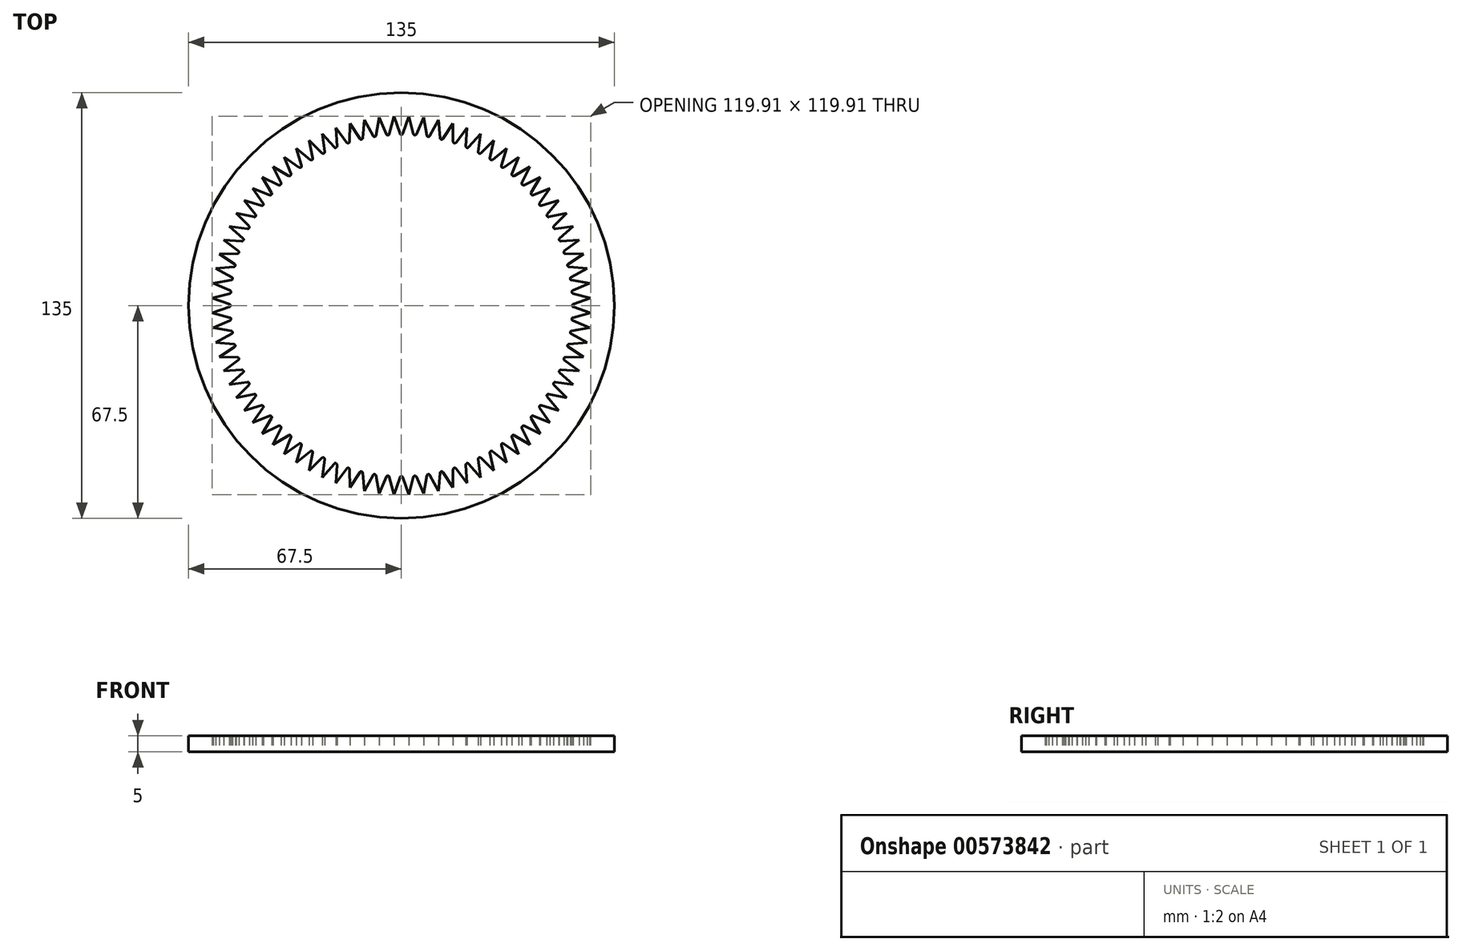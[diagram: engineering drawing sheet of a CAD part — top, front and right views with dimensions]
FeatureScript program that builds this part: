
annotation { "Feature Type Name" : "Feature", "Feature Type Description" : "" }
export const myFeature = defineFeature(function(context is Context, id is Id, definition is map)
    precondition{}
    {
        {
            var Q0;
            Q0=qCreatedBy(makeId("Top.planeOp"),FACE);
            var sketch = newSketch(context, id + "F0", { "sketchPlane" : qUnion([Q0])});
            skLineSegment(sketch, "E0", {"start": v(-2.35, 59.95) * mm, "end": v(-0.47, 54.5) * mm});
            skLineSegment(sketch, "E1", {"start": v(0.47, 54.5) * mm, "end": v(2.36, 59.95) * mm});
            skPoint(sketch, "E2", {"position": v(0, 60) * mm});
            skCircle(sketch, "E3", {"center": v(0, 0) * mm, "radius": 67.5 * mm});
            skPoint(sketch, "E4.visualSharp", {"position": v(0, 53.14) * mm});
            skArc(sketch, "E4.filletArc", {"start": v(-0.47, 54.5) * mm, "mid": v(0, 54.17) * mm, "end": v(0.47, 54.5) * mm});
            skLineSegment(sketch, "E5.1.0", {"start": v(-3.8, 54.38) * mm, "end": v(-2.36, 59.95) * mm});
            skLineSegment(sketch, "E5.1.1", {"start": v(-7.05, 59.58) * mm, "end": v(-4.75, 54.3) * mm});
            skArc(sketch, "E5.1.2", {"start": v(-4.75, 54.3) * mm, "mid": v(-4.25, 54) * mm, "end": v(-3.8, 54.38) * mm});
            skLineSegment(sketch, "E5.2.0", {"start": v(-8.06, 53.9) * mm, "end": v(-7.05, 59.58) * mm});
            skLineSegment(sketch, "E5.2.1", {"start": v(-11.7, 58.85) * mm, "end": v(-9, 53.76) * mm});
            skArc(sketch, "E5.2.2", {"start": v(-9, 53.76) * mm, "mid": v(-8.47, 53.5) * mm, "end": v(-8.06, 53.9) * mm});
            skLineSegment(sketch, "E5.3.0", {"start": v(-12.26, 53.11) * mm, "end": v(-11.7, 58.85) * mm});
            skLineSegment(sketch, "E5.3.1", {"start": v(-16.29, 57.75) * mm, "end": v(-13.18, 52.9) * mm});
            skArc(sketch, "E5.3.2", {"start": v(-13.18, 52.9) * mm, "mid": v(-12.65, 52.67) * mm, "end": v(-12.26, 53.11) * mm});
            skLineSegment(sketch, "E5.4.0", {"start": v(-16.4, 51.98) * mm, "end": v(-16.29, 57.75) * mm});
            skLineSegment(sketch, "E5.4.1", {"start": v(-20.77, 56.3) * mm, "end": v(-17.3, 51.7) * mm});
            skArc(sketch, "E5.4.2", {"start": v(-17.3, 51.7) * mm, "mid": v(-16.74, 51.52) * mm, "end": v(-16.4, 51.98) * mm});
            skLineSegment(sketch, "E5.5.0", {"start": v(-20.42, 50.54) * mm, "end": v(-20.77, 56.3) * mm});
            skLineSegment(sketch, "E5.5.1", {"start": v(-25.12, 54.49) * mm, "end": v(-21.3, 50.18) * mm});
            skArc(sketch, "E5.5.2", {"start": v(-21.3, 50.18) * mm, "mid": v(-20.73, 50.05) * mm, "end": v(-20.42, 50.54) * mm});
            skLineSegment(sketch, "E5.6.0", {"start": v(-24.32, 48.78) * mm, "end": v(-25.12, 54.49) * mm});
            skLineSegment(sketch, "E5.6.1", {"start": v(-29.32, 52.35) * mm, "end": v(-25.17, 48.35) * mm});
            skArc(sketch, "E5.6.2", {"start": v(-25.17, 48.35) * mm, "mid": v(-24.6, 48.27) * mm, "end": v(-24.32, 48.78) * mm});
            skLineSegment(sketch, "E5.7.0", {"start": v(-28.08, 46.72) * mm, "end": v(-29.32, 52.35) * mm});
            skLineSegment(sketch, "E5.7.1", {"start": v(-33.33, 49.89) * mm, "end": v(-28.88, 46.23) * mm});
            skArc(sketch, "E5.7.2", {"start": v(-28.88, 46.23) * mm, "mid": v(-28.3, 46.19) * mm, "end": v(-28.08, 46.72) * mm});
            skLineSegment(sketch, "E5.8.0", {"start": v(-31.66, 44.37) * mm, "end": v(-33.33, 49.89) * mm});
            skLineSegment(sketch, "E5.8.1", {"start": v(-37.15, 47.12) * mm, "end": v(-32.42, 43.82) * mm});
            skArc(sketch, "E5.8.2", {"start": v(-32.42, 43.82) * mm, "mid": v(-31.84, 43.82) * mm, "end": v(-31.66, 44.37) * mm});
            skLineSegment(sketch, "E5.9.0", {"start": v(-35.04, 41.75) * mm, "end": v(-37.15, 47.12) * mm});
            skLineSegment(sketch, "E5.9.1", {"start": v(-40.73, 44.06) * mm, "end": v(-35.76, 41.14) * mm});
            skArc(sketch, "E5.9.2", {"start": v(-35.76, 41.14) * mm, "mid": v(-35.18, 41.2) * mm, "end": v(-35.04, 41.75) * mm});
            skLineSegment(sketch, "E5.10.0", {"start": v(-38.2, 38.88) * mm, "end": v(-40.73, 44.06) * mm});
            skLineSegment(sketch, "E5.10.1", {"start": v(-44.06, 40.73) * mm, "end": v(-38.88, 38.2) * mm});
            skArc(sketch, "E5.10.2", {"start": v(-38.88, 38.2) * mm, "mid": v(-38.3, 38.3) * mm, "end": v(-38.2, 38.88) * mm});
            skLineSegment(sketch, "E5.11.0", {"start": v(-41.14, 35.76) * mm, "end": v(-44.06, 40.73) * mm});
            skLineSegment(sketch, "E5.11.1", {"start": v(-47.12, 37.15) * mm, "end": v(-41.75, 35.04) * mm});
            skArc(sketch, "E5.11.2", {"start": v(-41.75, 35.04) * mm, "mid": v(-41.2, 35.18) * mm, "end": v(-41.14, 35.76) * mm});
            skLineSegment(sketch, "E5.12.0", {"start": v(-43.82, 32.42) * mm, "end": v(-47.12, 37.15) * mm});
            skLineSegment(sketch, "E5.12.1", {"start": v(-49.89, 33.33) * mm, "end": v(-44.37, 31.66) * mm});
            skArc(sketch, "E5.12.2", {"start": v(-44.37, 31.66) * mm, "mid": v(-43.82, 31.84) * mm, "end": v(-43.82, 32.42) * mm});
            skLineSegment(sketch, "E5.13.0", {"start": v(-46.23, 28.88) * mm, "end": v(-49.89, 33.33) * mm});
            skLineSegment(sketch, "E5.13.1", {"start": v(-52.35, 29.32) * mm, "end": v(-46.72, 28.08) * mm});
            skArc(sketch, "E5.13.2", {"start": v(-46.72, 28.08) * mm, "mid": v(-46.19, 28.3) * mm, "end": v(-46.23, 28.88) * mm});
            skLineSegment(sketch, "E5.14.0", {"start": v(-48.35, 25.17) * mm, "end": v(-52.35, 29.32) * mm});
            skLineSegment(sketch, "E5.14.1", {"start": v(-54.49, 25.12) * mm, "end": v(-48.78, 24.32) * mm});
            skArc(sketch, "E5.14.2", {"start": v(-48.78, 24.32) * mm, "mid": v(-48.27, 24.6) * mm, "end": v(-48.35, 25.17) * mm});
            skLineSegment(sketch, "E5.15.0", {"start": v(-50.18, 21.3) * mm, "end": v(-54.49, 25.12) * mm});
            skLineSegment(sketch, "E5.15.1", {"start": v(-56.3, 20.77) * mm, "end": v(-50.54, 20.42) * mm});
            skArc(sketch, "E5.15.2", {"start": v(-50.54, 20.42) * mm, "mid": v(-50.05, 20.73) * mm, "end": v(-50.18, 21.3) * mm});
            skLineSegment(sketch, "E5.16.0", {"start": v(-51.7, 17.3) * mm, "end": v(-56.3, 20.77) * mm});
            skLineSegment(sketch, "E5.16.1", {"start": v(-57.75, 16.29) * mm, "end": v(-51.98, 16.4) * mm});
            skArc(sketch, "E5.16.2", {"start": v(-51.98, 16.4) * mm, "mid": v(-51.52, 16.74) * mm, "end": v(-51.7, 17.3) * mm});
            skLineSegment(sketch, "E5.17.0", {"start": v(-52.9, 13.18) * mm, "end": v(-57.75, 16.29) * mm});
            skLineSegment(sketch, "E5.17.1", {"start": v(-58.85, 11.7) * mm, "end": v(-53.11, 12.26) * mm});
            skArc(sketch, "E5.17.2", {"start": v(-53.11, 12.26) * mm, "mid": v(-52.67, 12.65) * mm, "end": v(-52.9, 13.18) * mm});
            skLineSegment(sketch, "E5.18.0", {"start": v(-53.76, 9) * mm, "end": v(-58.85, 11.7) * mm});
            skLineSegment(sketch, "E5.18.1", {"start": v(-59.58, 7.05) * mm, "end": v(-53.9, 8.06) * mm});
            skArc(sketch, "E5.18.2", {"start": v(-53.9, 8.06) * mm, "mid": v(-53.5, 8.47) * mm, "end": v(-53.76, 9) * mm});
            skLineSegment(sketch, "E5.19.0", {"start": v(-54.3, 4.75) * mm, "end": v(-59.58, 7.05) * mm});
            skLineSegment(sketch, "E5.19.1", {"start": v(-59.95, 2.36) * mm, "end": v(-54.38, 3.8) * mm});
            skArc(sketch, "E5.19.2", {"start": v(-54.38, 3.8) * mm, "mid": v(-54, 4.25) * mm, "end": v(-54.3, 4.75) * mm});
            skLineSegment(sketch, "E5.20.0", {"start": v(-54.5, 0.47) * mm, "end": v(-59.95, 2.36) * mm});
            skLineSegment(sketch, "E5.20.1", {"start": v(-59.95, -2.35) * mm, "end": v(-54.5, -0.47) * mm});
            skArc(sketch, "E5.20.2", {"start": v(-54.5, -0.47) * mm, "mid": v(-54.17, 0) * mm, "end": v(-54.5, 0.47) * mm});
            skLineSegment(sketch, "E5.21.0", {"start": v(-54.38, -3.8) * mm, "end": v(-59.95, -2.36) * mm});
            skLineSegment(sketch, "E5.21.1", {"start": v(-59.58, -7.05) * mm, "end": v(-54.3, -4.75) * mm});
            skArc(sketch, "E5.21.2", {"start": v(-54.3, -4.75) * mm, "mid": v(-54, -4.25) * mm, "end": v(-54.38, -3.8) * mm});
            skLineSegment(sketch, "E5.22.0", {"start": v(-53.9, -8.06) * mm, "end": v(-59.58, -7.05) * mm});
            skLineSegment(sketch, "E5.22.1", {"start": v(-58.85, -11.7) * mm, "end": v(-53.76, -9) * mm});
            skArc(sketch, "E5.22.2", {"start": v(-53.76, -9) * mm, "mid": v(-53.5, -8.47) * mm, "end": v(-53.9, -8.06) * mm});
            skLineSegment(sketch, "E5.23.0", {"start": v(-53.11, -12.26) * mm, "end": v(-58.85, -11.7) * mm});
            skLineSegment(sketch, "E5.23.1", {"start": v(-57.75, -16.29) * mm, "end": v(-52.9, -13.18) * mm});
            skArc(sketch, "E5.23.2", {"start": v(-52.9, -13.18) * mm, "mid": v(-52.67, -12.65) * mm, "end": v(-53.11, -12.26) * mm});
            skLineSegment(sketch, "E5.24.0", {"start": v(-51.98, -16.4) * mm, "end": v(-57.75, -16.29) * mm});
            skLineSegment(sketch, "E5.24.1", {"start": v(-56.3, -20.77) * mm, "end": v(-51.7, -17.3) * mm});
            skArc(sketch, "E5.24.2", {"start": v(-51.7, -17.3) * mm, "mid": v(-51.52, -16.74) * mm, "end": v(-51.98, -16.4) * mm});
            skLineSegment(sketch, "E5.25.0", {"start": v(-50.54, -20.42) * mm, "end": v(-56.3, -20.77) * mm});
            skLineSegment(sketch, "E5.25.1", {"start": v(-54.49, -25.12) * mm, "end": v(-50.18, -21.3) * mm});
            skArc(sketch, "E5.25.2", {"start": v(-50.18, -21.3) * mm, "mid": v(-50.05, -20.73) * mm, "end": v(-50.54, -20.42) * mm});
            skLineSegment(sketch, "E5.26.0", {"start": v(-48.78, -24.32) * mm, "end": v(-54.49, -25.12) * mm});
            skLineSegment(sketch, "E5.26.1", {"start": v(-52.35, -29.32) * mm, "end": v(-48.35, -25.17) * mm});
            skArc(sketch, "E5.26.2", {"start": v(-48.35, -25.17) * mm, "mid": v(-48.27, -24.6) * mm, "end": v(-48.78, -24.32) * mm});
            skLineSegment(sketch, "E5.27.0", {"start": v(-46.72, -28.08) * mm, "end": v(-52.35, -29.32) * mm});
            skLineSegment(sketch, "E5.27.1", {"start": v(-49.89, -33.33) * mm, "end": v(-46.23, -28.88) * mm});
            skArc(sketch, "E5.27.2", {"start": v(-46.23, -28.88) * mm, "mid": v(-46.19, -28.3) * mm, "end": v(-46.72, -28.08) * mm});
            skLineSegment(sketch, "E5.28.0", {"start": v(-44.37, -31.66) * mm, "end": v(-49.89, -33.33) * mm});
            skLineSegment(sketch, "E5.28.1", {"start": v(-47.12, -37.15) * mm, "end": v(-43.82, -32.42) * mm});
            skArc(sketch, "E5.28.2", {"start": v(-43.82, -32.42) * mm, "mid": v(-43.82, -31.84) * mm, "end": v(-44.37, -31.66) * mm});
            skLineSegment(sketch, "E5.29.0", {"start": v(-41.75, -35.04) * mm, "end": v(-47.12, -37.15) * mm});
            skLineSegment(sketch, "E5.29.1", {"start": v(-44.06, -40.73) * mm, "end": v(-41.14, -35.76) * mm});
            skArc(sketch, "E5.29.2", {"start": v(-41.14, -35.76) * mm, "mid": v(-41.2, -35.18) * mm, "end": v(-41.75, -35.04) * mm});
            skLineSegment(sketch, "E5.30.0", {"start": v(-38.88, -38.2) * mm, "end": v(-44.06, -40.73) * mm});
            skLineSegment(sketch, "E5.30.1", {"start": v(-40.73, -44.06) * mm, "end": v(-38.2, -38.88) * mm});
            skArc(sketch, "E5.30.2", {"start": v(-38.2, -38.88) * mm, "mid": v(-38.3, -38.3) * mm, "end": v(-38.88, -38.2) * mm});
            skLineSegment(sketch, "E5.31.0", {"start": v(-35.76, -41.14) * mm, "end": v(-40.73, -44.06) * mm});
            skLineSegment(sketch, "E5.31.1", {"start": v(-37.15, -47.12) * mm, "end": v(-35.04, -41.75) * mm});
            skArc(sketch, "E5.31.2", {"start": v(-35.04, -41.75) * mm, "mid": v(-35.18, -41.2) * mm, "end": v(-35.76, -41.14) * mm});
            skLineSegment(sketch, "E5.32.0", {"start": v(-32.42, -43.82) * mm, "end": v(-37.15, -47.12) * mm});
            skLineSegment(sketch, "E5.32.1", {"start": v(-33.33, -49.89) * mm, "end": v(-31.66, -44.37) * mm});
            skArc(sketch, "E5.32.2", {"start": v(-31.66, -44.37) * mm, "mid": v(-31.84, -43.82) * mm, "end": v(-32.42, -43.82) * mm});
            skLineSegment(sketch, "E5.33.0", {"start": v(-28.88, -46.23) * mm, "end": v(-33.33, -49.89) * mm});
            skLineSegment(sketch, "E5.33.1", {"start": v(-29.32, -52.35) * mm, "end": v(-28.08, -46.72) * mm});
            skArc(sketch, "E5.33.2", {"start": v(-28.08, -46.72) * mm, "mid": v(-28.3, -46.19) * mm, "end": v(-28.88, -46.23) * mm});
            skLineSegment(sketch, "E5.34.0", {"start": v(-25.17, -48.35) * mm, "end": v(-29.32, -52.35) * mm});
            skLineSegment(sketch, "E5.34.1", {"start": v(-25.12, -54.49) * mm, "end": v(-24.32, -48.78) * mm});
            skArc(sketch, "E5.34.2", {"start": v(-24.32, -48.78) * mm, "mid": v(-24.6, -48.27) * mm, "end": v(-25.17, -48.35) * mm});
            skLineSegment(sketch, "E5.35.0", {"start": v(-21.3, -50.18) * mm, "end": v(-25.12, -54.49) * mm});
            skLineSegment(sketch, "E5.35.1", {"start": v(-20.77, -56.3) * mm, "end": v(-20.42, -50.54) * mm});
            skArc(sketch, "E5.35.2", {"start": v(-20.42, -50.54) * mm, "mid": v(-20.73, -50.05) * mm, "end": v(-21.3, -50.18) * mm});
            skLineSegment(sketch, "E5.36.0", {"start": v(-17.3, -51.7) * mm, "end": v(-20.77, -56.3) * mm});
            skLineSegment(sketch, "E5.36.1", {"start": v(-16.29, -57.75) * mm, "end": v(-16.4, -51.98) * mm});
            skArc(sketch, "E5.36.2", {"start": v(-16.4, -51.98) * mm, "mid": v(-16.74, -51.52) * mm, "end": v(-17.3, -51.7) * mm});
            skLineSegment(sketch, "E5.37.0", {"start": v(-13.18, -52.9) * mm, "end": v(-16.29, -57.75) * mm});
            skLineSegment(sketch, "E5.37.1", {"start": v(-11.7, -58.85) * mm, "end": v(-12.26, -53.11) * mm});
            skArc(sketch, "E5.37.2", {"start": v(-12.26, -53.11) * mm, "mid": v(-12.65, -52.67) * mm, "end": v(-13.18, -52.9) * mm});
            skLineSegment(sketch, "E5.38.0", {"start": v(-9, -53.76) * mm, "end": v(-11.7, -58.85) * mm});
            skLineSegment(sketch, "E5.38.1", {"start": v(-7.05, -59.58) * mm, "end": v(-8.06, -53.9) * mm});
            skArc(sketch, "E5.38.2", {"start": v(-8.06, -53.9) * mm, "mid": v(-8.47, -53.5) * mm, "end": v(-9, -53.76) * mm});
            skLineSegment(sketch, "E5.39.0", {"start": v(-4.75, -54.3) * mm, "end": v(-7.05, -59.58) * mm});
            skLineSegment(sketch, "E5.39.1", {"start": v(-2.36, -59.95) * mm, "end": v(-3.8, -54.38) * mm});
            skArc(sketch, "E5.39.2", {"start": v(-3.8, -54.38) * mm, "mid": v(-4.25, -54) * mm, "end": v(-4.75, -54.3) * mm});
            skLineSegment(sketch, "E5.40.0", {"start": v(-0.47, -54.5) * mm, "end": v(-2.36, -59.95) * mm});
            skLineSegment(sketch, "E5.40.1", {"start": v(2.35, -59.95) * mm, "end": v(0.47, -54.5) * mm});
            skArc(sketch, "E5.40.2", {"start": v(0.47, -54.5) * mm, "mid": v(0, -54.17) * mm, "end": v(-0.47, -54.5) * mm});
            skLineSegment(sketch, "E5.41.0", {"start": v(3.8, -54.38) * mm, "end": v(2.36, -59.95) * mm});
            skLineSegment(sketch, "E5.41.1", {"start": v(7.05, -59.58) * mm, "end": v(4.75, -54.3) * mm});
            skArc(sketch, "E5.41.2", {"start": v(4.75, -54.3) * mm, "mid": v(4.25, -54) * mm, "end": v(3.8, -54.38) * mm});
            skLineSegment(sketch, "E5.42.0", {"start": v(8.06, -53.9) * mm, "end": v(7.05, -59.58) * mm});
            skLineSegment(sketch, "E5.42.1", {"start": v(11.7, -58.85) * mm, "end": v(9, -53.76) * mm});
            skArc(sketch, "E5.42.2", {"start": v(9, -53.76) * mm, "mid": v(8.47, -53.5) * mm, "end": v(8.06, -53.9) * mm});
            skLineSegment(sketch, "E5.43.0", {"start": v(12.26, -53.11) * mm, "end": v(11.7, -58.85) * mm});
            skLineSegment(sketch, "E5.43.1", {"start": v(16.29, -57.75) * mm, "end": v(13.18, -52.9) * mm});
            skArc(sketch, "E5.43.2", {"start": v(13.18, -52.9) * mm, "mid": v(12.65, -52.67) * mm, "end": v(12.26, -53.11) * mm});
            skLineSegment(sketch, "E5.44.0", {"start": v(16.4, -51.98) * mm, "end": v(16.29, -57.75) * mm});
            skLineSegment(sketch, "E5.44.1", {"start": v(20.77, -56.3) * mm, "end": v(17.3, -51.7) * mm});
            skArc(sketch, "E5.44.2", {"start": v(17.3, -51.7) * mm, "mid": v(16.74, -51.52) * mm, "end": v(16.4, -51.98) * mm});
            skLineSegment(sketch, "E5.45.0", {"start": v(20.42, -50.54) * mm, "end": v(20.77, -56.3) * mm});
            skLineSegment(sketch, "E5.45.1", {"start": v(25.12, -54.49) * mm, "end": v(21.3, -50.18) * mm});
            skArc(sketch, "E5.45.2", {"start": v(21.3, -50.18) * mm, "mid": v(20.73, -50.05) * mm, "end": v(20.42, -50.54) * mm});
            skLineSegment(sketch, "E5.46.0", {"start": v(24.32, -48.78) * mm, "end": v(25.12, -54.49) * mm});
            skLineSegment(sketch, "E5.46.1", {"start": v(29.32, -52.35) * mm, "end": v(25.17, -48.35) * mm});
            skArc(sketch, "E5.46.2", {"start": v(25.17, -48.35) * mm, "mid": v(24.6, -48.27) * mm, "end": v(24.32, -48.78) * mm});
            skLineSegment(sketch, "E5.47.0", {"start": v(28.08, -46.72) * mm, "end": v(29.32, -52.35) * mm});
            skLineSegment(sketch, "E5.47.1", {"start": v(33.33, -49.89) * mm, "end": v(28.88, -46.23) * mm});
            skArc(sketch, "E5.47.2", {"start": v(28.88, -46.23) * mm, "mid": v(28.3, -46.19) * mm, "end": v(28.08, -46.72) * mm});
            skLineSegment(sketch, "E5.48.0", {"start": v(31.66, -44.37) * mm, "end": v(33.33, -49.89) * mm});
            skLineSegment(sketch, "E5.48.1", {"start": v(37.15, -47.12) * mm, "end": v(32.42, -43.82) * mm});
            skArc(sketch, "E5.48.2", {"start": v(32.42, -43.82) * mm, "mid": v(31.84, -43.82) * mm, "end": v(31.66, -44.37) * mm});
            skLineSegment(sketch, "E5.49.0", {"start": v(35.04, -41.75) * mm, "end": v(37.15, -47.12) * mm});
            skLineSegment(sketch, "E5.49.1", {"start": v(40.73, -44.06) * mm, "end": v(35.76, -41.14) * mm});
            skArc(sketch, "E5.49.2", {"start": v(35.76, -41.14) * mm, "mid": v(35.18, -41.2) * mm, "end": v(35.04, -41.75) * mm});
            skLineSegment(sketch, "E5.50.0", {"start": v(38.2, -38.88) * mm, "end": v(40.73, -44.06) * mm});
            skLineSegment(sketch, "E5.50.1", {"start": v(44.06, -40.73) * mm, "end": v(38.88, -38.2) * mm});
            skArc(sketch, "E5.50.2", {"start": v(38.88, -38.2) * mm, "mid": v(38.3, -38.3) * mm, "end": v(38.2, -38.88) * mm});
            skLineSegment(sketch, "E5.51.0", {"start": v(41.14, -35.76) * mm, "end": v(44.06, -40.73) * mm});
            skLineSegment(sketch, "E5.51.1", {"start": v(47.12, -37.15) * mm, "end": v(41.75, -35.04) * mm});
            skArc(sketch, "E5.51.2", {"start": v(41.75, -35.04) * mm, "mid": v(41.2, -35.18) * mm, "end": v(41.14, -35.76) * mm});
            skLineSegment(sketch, "E5.52.0", {"start": v(43.82, -32.42) * mm, "end": v(47.12, -37.15) * mm});
            skLineSegment(sketch, "E5.52.1", {"start": v(49.89, -33.33) * mm, "end": v(44.37, -31.66) * mm});
            skArc(sketch, "E5.52.2", {"start": v(44.37, -31.66) * mm, "mid": v(43.82, -31.84) * mm, "end": v(43.82, -32.42) * mm});
            skLineSegment(sketch, "E5.53.0", {"start": v(46.23, -28.88) * mm, "end": v(49.89, -33.33) * mm});
            skLineSegment(sketch, "E5.53.1", {"start": v(52.35, -29.32) * mm, "end": v(46.72, -28.08) * mm});
            skArc(sketch, "E5.53.2", {"start": v(46.72, -28.08) * mm, "mid": v(46.19, -28.3) * mm, "end": v(46.23, -28.88) * mm});
            skLineSegment(sketch, "E5.54.0", {"start": v(48.35, -25.17) * mm, "end": v(52.35, -29.32) * mm});
            skLineSegment(sketch, "E5.54.1", {"start": v(54.49, -25.12) * mm, "end": v(48.78, -24.32) * mm});
            skArc(sketch, "E5.54.2", {"start": v(48.78, -24.32) * mm, "mid": v(48.27, -24.6) * mm, "end": v(48.35, -25.17) * mm});
            skLineSegment(sketch, "E5.55.0", {"start": v(50.18, -21.3) * mm, "end": v(54.49, -25.12) * mm});
            skLineSegment(sketch, "E5.55.1", {"start": v(56.3, -20.77) * mm, "end": v(50.54, -20.42) * mm});
            skArc(sketch, "E5.55.2", {"start": v(50.54, -20.42) * mm, "mid": v(50.05, -20.73) * mm, "end": v(50.18, -21.3) * mm});
            skLineSegment(sketch, "E5.56.0", {"start": v(51.7, -17.3) * mm, "end": v(56.3, -20.77) * mm});
            skLineSegment(sketch, "E5.56.1", {"start": v(57.75, -16.29) * mm, "end": v(51.98, -16.4) * mm});
            skArc(sketch, "E5.56.2", {"start": v(51.98, -16.4) * mm, "mid": v(51.52, -16.74) * mm, "end": v(51.7, -17.3) * mm});
            skLineSegment(sketch, "E5.57.0", {"start": v(52.9, -13.18) * mm, "end": v(57.75, -16.29) * mm});
            skLineSegment(sketch, "E5.57.1", {"start": v(58.85, -11.7) * mm, "end": v(53.11, -12.26) * mm});
            skArc(sketch, "E5.57.2", {"start": v(53.11, -12.26) * mm, "mid": v(52.67, -12.65) * mm, "end": v(52.9, -13.18) * mm});
            skLineSegment(sketch, "E5.58.0", {"start": v(53.76, -9) * mm, "end": v(58.85, -11.7) * mm});
            skLineSegment(sketch, "E5.58.1", {"start": v(59.58, -7.05) * mm, "end": v(53.9, -8.06) * mm});
            skArc(sketch, "E5.58.2", {"start": v(53.9, -8.06) * mm, "mid": v(53.5, -8.47) * mm, "end": v(53.76, -9) * mm});
            skLineSegment(sketch, "E5.59.0", {"start": v(54.3, -4.75) * mm, "end": v(59.58, -7.05) * mm});
            skLineSegment(sketch, "E5.59.1", {"start": v(59.95, -2.36) * mm, "end": v(54.38, -3.8) * mm});
            skArc(sketch, "E5.59.2", {"start": v(54.38, -3.8) * mm, "mid": v(54, -4.25) * mm, "end": v(54.3, -4.75) * mm});
            skLineSegment(sketch, "E5.60.0", {"start": v(54.5, -0.47) * mm, "end": v(59.95, -2.36) * mm});
            skLineSegment(sketch, "E5.60.1", {"start": v(59.95, 2.35) * mm, "end": v(54.5, 0.47) * mm});
            skArc(sketch, "E5.60.2", {"start": v(54.5, 0.47) * mm, "mid": v(54.17, 0) * mm, "end": v(54.5, -0.47) * mm});
            skLineSegment(sketch, "E5.61.0", {"start": v(54.38, 3.8) * mm, "end": v(59.95, 2.36) * mm});
            skLineSegment(sketch, "E5.61.1", {"start": v(59.58, 7.05) * mm, "end": v(54.3, 4.75) * mm});
            skArc(sketch, "E5.61.2", {"start": v(54.3, 4.75) * mm, "mid": v(54, 4.25) * mm, "end": v(54.38, 3.8) * mm});
            skLineSegment(sketch, "E5.62.0", {"start": v(53.9, 8.06) * mm, "end": v(59.58, 7.05) * mm});
            skLineSegment(sketch, "E5.62.1", {"start": v(58.85, 11.7) * mm, "end": v(53.76, 9) * mm});
            skArc(sketch, "E5.62.2", {"start": v(53.76, 9) * mm, "mid": v(53.5, 8.47) * mm, "end": v(53.9, 8.06) * mm});
            skLineSegment(sketch, "E5.63.0", {"start": v(53.11, 12.26) * mm, "end": v(58.85, 11.7) * mm});
            skLineSegment(sketch, "E5.63.1", {"start": v(57.75, 16.29) * mm, "end": v(52.9, 13.18) * mm});
            skArc(sketch, "E5.63.2", {"start": v(52.9, 13.18) * mm, "mid": v(52.67, 12.65) * mm, "end": v(53.11, 12.26) * mm});
            skLineSegment(sketch, "E5.64.0", {"start": v(51.98, 16.4) * mm, "end": v(57.75, 16.29) * mm});
            skLineSegment(sketch, "E5.64.1", {"start": v(56.3, 20.77) * mm, "end": v(51.7, 17.3) * mm});
            skArc(sketch, "E5.64.2", {"start": v(51.7, 17.3) * mm, "mid": v(51.52, 16.74) * mm, "end": v(51.98, 16.4) * mm});
            skLineSegment(sketch, "E5.65.0", {"start": v(50.54, 20.42) * mm, "end": v(56.3, 20.77) * mm});
            skLineSegment(sketch, "E5.65.1", {"start": v(54.49, 25.12) * mm, "end": v(50.18, 21.3) * mm});
            skArc(sketch, "E5.65.2", {"start": v(50.18, 21.3) * mm, "mid": v(50.05, 20.73) * mm, "end": v(50.54, 20.42) * mm});
            skLineSegment(sketch, "E5.66.0", {"start": v(48.78, 24.32) * mm, "end": v(54.49, 25.12) * mm});
            skLineSegment(sketch, "E5.66.1", {"start": v(52.35, 29.32) * mm, "end": v(48.35, 25.17) * mm});
            skArc(sketch, "E5.66.2", {"start": v(48.35, 25.17) * mm, "mid": v(48.27, 24.6) * mm, "end": v(48.78, 24.32) * mm});
            skLineSegment(sketch, "E5.67.0", {"start": v(46.72, 28.08) * mm, "end": v(52.35, 29.32) * mm});
            skLineSegment(sketch, "E5.67.1", {"start": v(49.89, 33.33) * mm, "end": v(46.23, 28.88) * mm});
            skArc(sketch, "E5.67.2", {"start": v(46.23, 28.88) * mm, "mid": v(46.19, 28.3) * mm, "end": v(46.72, 28.08) * mm});
            skLineSegment(sketch, "E5.68.0", {"start": v(44.37, 31.66) * mm, "end": v(49.89, 33.33) * mm});
            skLineSegment(sketch, "E5.68.1", {"start": v(47.12, 37.15) * mm, "end": v(43.82, 32.42) * mm});
            skArc(sketch, "E5.68.2", {"start": v(43.82, 32.42) * mm, "mid": v(43.82, 31.84) * mm, "end": v(44.37, 31.66) * mm});
            skLineSegment(sketch, "E5.69.0", {"start": v(41.75, 35.04) * mm, "end": v(47.12, 37.15) * mm});
            skLineSegment(sketch, "E5.69.1", {"start": v(44.06, 40.73) * mm, "end": v(41.14, 35.76) * mm});
            skArc(sketch, "E5.69.2", {"start": v(41.14, 35.76) * mm, "mid": v(41.2, 35.18) * mm, "end": v(41.75, 35.04) * mm});
            skLineSegment(sketch, "E5.70.0", {"start": v(38.88, 38.2) * mm, "end": v(44.06, 40.73) * mm});
            skLineSegment(sketch, "E5.70.1", {"start": v(40.73, 44.06) * mm, "end": v(38.2, 38.88) * mm});
            skArc(sketch, "E5.70.2", {"start": v(38.2, 38.88) * mm, "mid": v(38.3, 38.3) * mm, "end": v(38.88, 38.2) * mm});
            skLineSegment(sketch, "E5.71.0", {"start": v(35.76, 41.14) * mm, "end": v(40.73, 44.06) * mm});
            skLineSegment(sketch, "E5.71.1", {"start": v(37.15, 47.12) * mm, "end": v(35.04, 41.75) * mm});
            skArc(sketch, "E5.71.2", {"start": v(35.04, 41.75) * mm, "mid": v(35.18, 41.2) * mm, "end": v(35.76, 41.14) * mm});
            skLineSegment(sketch, "E5.72.0", {"start": v(32.42, 43.82) * mm, "end": v(37.15, 47.12) * mm});
            skLineSegment(sketch, "E5.72.1", {"start": v(33.33, 49.89) * mm, "end": v(31.66, 44.37) * mm});
            skArc(sketch, "E5.72.2", {"start": v(31.66, 44.37) * mm, "mid": v(31.84, 43.82) * mm, "end": v(32.42, 43.82) * mm});
            skLineSegment(sketch, "E5.73.0", {"start": v(28.88, 46.23) * mm, "end": v(33.33, 49.89) * mm});
            skLineSegment(sketch, "E5.73.1", {"start": v(29.32, 52.35) * mm, "end": v(28.08, 46.72) * mm});
            skArc(sketch, "E5.73.2", {"start": v(28.08, 46.72) * mm, "mid": v(28.3, 46.19) * mm, "end": v(28.88, 46.23) * mm});
            skLineSegment(sketch, "E5.74.0", {"start": v(25.17, 48.35) * mm, "end": v(29.32, 52.35) * mm});
            skLineSegment(sketch, "E5.74.1", {"start": v(25.12, 54.49) * mm, "end": v(24.32, 48.78) * mm});
            skArc(sketch, "E5.74.2", {"start": v(24.32, 48.78) * mm, "mid": v(24.6, 48.27) * mm, "end": v(25.17, 48.35) * mm});
            skLineSegment(sketch, "E5.75.0", {"start": v(21.3, 50.18) * mm, "end": v(25.12, 54.49) * mm});
            skLineSegment(sketch, "E5.75.1", {"start": v(20.77, 56.3) * mm, "end": v(20.42, 50.54) * mm});
            skArc(sketch, "E5.75.2", {"start": v(20.42, 50.54) * mm, "mid": v(20.73, 50.05) * mm, "end": v(21.3, 50.18) * mm});
            skLineSegment(sketch, "E5.76.0", {"start": v(17.3, 51.7) * mm, "end": v(20.77, 56.3) * mm});
            skLineSegment(sketch, "E5.76.1", {"start": v(16.29, 57.75) * mm, "end": v(16.4, 51.98) * mm});
            skArc(sketch, "E5.76.2", {"start": v(16.4, 51.98) * mm, "mid": v(16.74, 51.52) * mm, "end": v(17.3, 51.7) * mm});
            skLineSegment(sketch, "E5.77.0", {"start": v(13.18, 52.9) * mm, "end": v(16.29, 57.75) * mm});
            skLineSegment(sketch, "E5.77.1", {"start": v(11.7, 58.85) * mm, "end": v(12.26, 53.11) * mm});
            skArc(sketch, "E5.77.2", {"start": v(12.26, 53.11) * mm, "mid": v(12.65, 52.67) * mm, "end": v(13.18, 52.9) * mm});
            skLineSegment(sketch, "E5.78.0", {"start": v(9, 53.76) * mm, "end": v(11.7, 58.85) * mm});
            skLineSegment(sketch, "E5.78.1", {"start": v(7.05, 59.58) * mm, "end": v(8.06, 53.9) * mm});
            skArc(sketch, "E5.78.2", {"start": v(8.06, 53.9) * mm, "mid": v(8.47, 53.5) * mm, "end": v(9, 53.76) * mm});
            skLineSegment(sketch, "E5.79.0", {"start": v(4.75, 54.3) * mm, "end": v(7.05, 59.58) * mm});
            skLineSegment(sketch, "E5.79.1", {"start": v(2.36, 59.95) * mm, "end": v(3.8, 54.38) * mm});
            skArc(sketch, "E5.79.2", {"start": v(3.8, 54.38) * mm, "mid": v(4.25, 54) * mm, "end": v(4.75, 54.3) * mm});
            skArc(sketch, "E6.trimOffspring", {"start": v(7.05, 59.58) * mm, "mid": v(7.05, 59.58) * mm, "end": v(7.05, 59.58) * mm});
            skArc(sketch, "E7.trimOffspring", {"start": v(11.7, 58.85) * mm, "mid": v(11.7, 58.85) * mm, "end": v(11.7, 58.85) * mm});
            skArc(sketch, "E8.trimOffspring", {"start": v(16.29, 57.75) * mm, "mid": v(16.29, 57.75) * mm, "end": v(16.29, 57.75) * mm});
            skArc(sketch, "E9.trimOffspring", {"start": v(20.77, 56.3) * mm, "mid": v(20.77, 56.3) * mm, "end": v(20.77, 56.3) * mm});
            skArc(sketch, "E10.trimOffspring", {"start": v(25.12, 54.49) * mm, "mid": v(25.12, 54.49) * mm, "end": v(25.12, 54.49) * mm});
            skCircle(sketch, "E11", {"center": v(0, 0) * mm, "radius": 60 * mm});
            skSolve(sketch);
        }
        {
            var Q0;
            Q0 = qSketchRegion(id + "F0", true);
            var Q1;
            {var subQ0=sQuery(id+"F0.wireOp",EDGE,"E0");Q1=makeQuery(id+"F0.imprint","IMPRINT",FACE,{"disambiguationData":[TD([[makeQuery(id+"F0.imprint","IMPRINT",EDGE,{"derivedFrom":subQ0}),1.0]])]});}
            var Q2;
            {var subQ0=sQuery(id+"F0.wireOp",EDGE,"E5.79.0");Q2=makeQuery(id+"F0.imprint","IMPRINT",FACE,{"disambiguationData":[TD([[makeQuery(id+"F0.imprint","IMPRINT",EDGE,{"derivedFrom":subQ0}),1.0]])]});}
            var Q3;
            {var subQ0=sQuery(id+"F0.wireOp",EDGE,"E5.78.0");Q3=makeQuery(id+"F0.imprint","IMPRINT",FACE,{"disambiguationData":[TD([[makeQuery(id+"F0.imprint","IMPRINT",EDGE,{"derivedFrom":subQ0}),1.0]])]});}
            var Q4;
            {var subQ0=sQuery(id+"F0.wireOp",EDGE,"E5.77.0");Q4=makeQuery(id+"F0.imprint","IMPRINT",FACE,{"disambiguationData":[TD([[makeQuery(id+"F0.imprint","IMPRINT",EDGE,{"derivedFrom":subQ0}),1.0]])]});}
            var Q5;
            {var subQ0=sQuery(id+"F0.wireOp",EDGE,"E5.76.0");Q5=makeQuery(id+"F0.imprint","IMPRINT",FACE,{"disambiguationData":[TD([[makeQuery(id+"F0.imprint","IMPRINT",EDGE,{"derivedFrom":subQ0}),1.0]])]});}
            var Q6;
            {var subQ0=sQuery(id+"F0.wireOp",EDGE,"E5.75.0");Q6=makeQuery(id+"F0.imprint","IMPRINT",FACE,{"disambiguationData":[TD([[makeQuery(id+"F0.imprint","IMPRINT",EDGE,{"derivedFrom":subQ0}),1.0]])]});}
            var Q7;
            {var subQ0=sQuery(id+"F0.wireOp",EDGE,"E5.74.0");Q7=makeQuery(id+"F0.imprint","IMPRINT",FACE,{"disambiguationData":[TD([[makeQuery(id+"F0.imprint","IMPRINT",EDGE,{"derivedFrom":subQ0}),1.0]])]});}
            var Q8;
            {var subQ0=sQuery(id+"F0.wireOp",EDGE,"E5.73.0");Q8=makeQuery(id+"F0.imprint","IMPRINT",FACE,{"disambiguationData":[TD([[makeQuery(id+"F0.imprint","IMPRINT",EDGE,{"derivedFrom":subQ0}),1.0]])]});}
            var Q9;
            {var subQ0=sQuery(id+"F0.wireOp",EDGE,"E5.72.0");Q9=makeQuery(id+"F0.imprint","IMPRINT",FACE,{"disambiguationData":[TD([[makeQuery(id+"F0.imprint","IMPRINT",EDGE,{"derivedFrom":subQ0}),1.0]])]});}
            var Q10;
            {var subQ0=sQuery(id+"F0.wireOp",EDGE,"E5.71.0");Q10=makeQuery(id+"F0.imprint","IMPRINT",FACE,{"disambiguationData":[TD([[makeQuery(id+"F0.imprint","IMPRINT",EDGE,{"derivedFrom":subQ0}),1.0]])]});}
            var Q11;
            {var subQ0=sQuery(id+"F0.wireOp",EDGE,"E5.70.0");Q11=makeQuery(id+"F0.imprint","IMPRINT",FACE,{"disambiguationData":[TD([[makeQuery(id+"F0.imprint","IMPRINT",EDGE,{"derivedFrom":subQ0}),1.0]])]});}
            var Q12;
            {var subQ0=sQuery(id+"F0.wireOp",EDGE,"E5.69.0");Q12=makeQuery(id+"F0.imprint","IMPRINT",FACE,{"disambiguationData":[TD([[makeQuery(id+"F0.imprint","IMPRINT",EDGE,{"derivedFrom":subQ0}),1.0]])]});}
            var Q13;
            {var subQ0=sQuery(id+"F0.wireOp",EDGE,"E5.68.0");Q13=makeQuery(id+"F0.imprint","IMPRINT",FACE,{"disambiguationData":[TD([[makeQuery(id+"F0.imprint","IMPRINT",EDGE,{"derivedFrom":subQ0}),1.0]])]});}
            var Q14;
            {var subQ0=sQuery(id+"F0.wireOp",EDGE,"E5.67.0");Q14=makeQuery(id+"F0.imprint","IMPRINT",FACE,{"disambiguationData":[TD([[makeQuery(id+"F0.imprint","IMPRINT",EDGE,{"derivedFrom":subQ0}),1.0]])]});}
            var Q15;
            {var subQ0=sQuery(id+"F0.wireOp",EDGE,"E5.65.0");Q15=makeQuery(id+"F0.imprint","IMPRINT",FACE,{"disambiguationData":[TD([[makeQuery(id+"F0.imprint","IMPRINT",EDGE,{"derivedFrom":subQ0}),1.0]])]});}
            var Q16;
            {var subQ0=sQuery(id+"F0.wireOp",EDGE,"E5.64.0");Q16=makeQuery(id+"F0.imprint","IMPRINT",FACE,{"disambiguationData":[TD([[makeQuery(id+"F0.imprint","IMPRINT",EDGE,{"derivedFrom":subQ0}),1.0]])]});}
            var Q17;
            {var subQ0=sQuery(id+"F0.wireOp",EDGE,"E5.63.0");Q17=makeQuery(id+"F0.imprint","IMPRINT",FACE,{"disambiguationData":[TD([[makeQuery(id+"F0.imprint","IMPRINT",EDGE,{"derivedFrom":subQ0}),1.0]])]});}
            var Q18;
            {var subQ0=sQuery(id+"F0.wireOp",EDGE,"E5.62.0");Q18=makeQuery(id+"F0.imprint","IMPRINT",FACE,{"disambiguationData":[TD([[makeQuery(id+"F0.imprint","IMPRINT",EDGE,{"derivedFrom":subQ0}),1.0]])]});}
            var Q19;
            {var subQ0=sQuery(id+"F0.wireOp",EDGE,"E5.61.0");Q19=makeQuery(id+"F0.imprint","IMPRINT",FACE,{"disambiguationData":[TD([[makeQuery(id+"F0.imprint","IMPRINT",EDGE,{"derivedFrom":subQ0}),1.0]])]});}
            var Q20;
            {var subQ0=sQuery(id+"F0.wireOp",EDGE,"E5.60.0");Q20=makeQuery(id+"F0.imprint","IMPRINT",FACE,{"disambiguationData":[TD([[makeQuery(id+"F0.imprint","IMPRINT",EDGE,{"derivedFrom":subQ0}),1.0]])]});}
            var Q21;
            {var subQ0=sQuery(id+"F0.wireOp",EDGE,"E5.59.0");Q21=makeQuery(id+"F0.imprint","IMPRINT",FACE,{"disambiguationData":[TD([[makeQuery(id+"F0.imprint","IMPRINT",EDGE,{"derivedFrom":subQ0}),1.0]])]});}
            var Q22;
            {var subQ0=sQuery(id+"F0.wireOp",EDGE,"E5.58.0");Q22=makeQuery(id+"F0.imprint","IMPRINT",FACE,{"disambiguationData":[TD([[makeQuery(id+"F0.imprint","IMPRINT",EDGE,{"derivedFrom":subQ0}),1.0]])]});}
            var Q23;
            {var subQ0=sQuery(id+"F0.wireOp",EDGE,"E5.57.0");Q23=makeQuery(id+"F0.imprint","IMPRINT",FACE,{"disambiguationData":[TD([[makeQuery(id+"F0.imprint","IMPRINT",EDGE,{"derivedFrom":subQ0}),1.0]])]});}
            var Q24;
            {var subQ0=sQuery(id+"F0.wireOp",EDGE,"E5.56.0");Q24=makeQuery(id+"F0.imprint","IMPRINT",FACE,{"disambiguationData":[TD([[makeQuery(id+"F0.imprint","IMPRINT",EDGE,{"derivedFrom":subQ0}),1.0]])]});}
            var Q25;
            {var subQ0=sQuery(id+"F0.wireOp",EDGE,"E5.55.0");Q25=makeQuery(id+"F0.imprint","IMPRINT",FACE,{"disambiguationData":[TD([[makeQuery(id+"F0.imprint","IMPRINT",EDGE,{"derivedFrom":subQ0}),1.0]])]});}
            var Q26;
            {var subQ0=sQuery(id+"F0.wireOp",EDGE,"E5.54.0");Q26=makeQuery(id+"F0.imprint","IMPRINT",FACE,{"disambiguationData":[TD([[makeQuery(id+"F0.imprint","IMPRINT",EDGE,{"derivedFrom":subQ0}),1.0]])]});}
            var Q27;
            {var subQ0=sQuery(id+"F0.wireOp",EDGE,"E5.53.0");Q27=makeQuery(id+"F0.imprint","IMPRINT",FACE,{"disambiguationData":[TD([[makeQuery(id+"F0.imprint","IMPRINT",EDGE,{"derivedFrom":subQ0}),1.0]])]});}
            var Q28;
            {var subQ0=sQuery(id+"F0.wireOp",EDGE,"E5.52.0");Q28=makeQuery(id+"F0.imprint","IMPRINT",FACE,{"disambiguationData":[TD([[makeQuery(id+"F0.imprint","IMPRINT",EDGE,{"derivedFrom":subQ0}),1.0]])]});}
            var Q29;
            {var subQ0=sQuery(id+"F0.wireOp",EDGE,"E5.51.0");Q29=makeQuery(id+"F0.imprint","IMPRINT",FACE,{"disambiguationData":[TD([[makeQuery(id+"F0.imprint","IMPRINT",EDGE,{"derivedFrom":subQ0}),1.0]])]});}
            var Q30;
            {var subQ0=sQuery(id+"F0.wireOp",EDGE,"E5.50.0");Q30=makeQuery(id+"F0.imprint","IMPRINT",FACE,{"disambiguationData":[TD([[makeQuery(id+"F0.imprint","IMPRINT",EDGE,{"derivedFrom":subQ0}),1.0]])]});}
            var Q31;
            {var subQ0=sQuery(id+"F0.wireOp",EDGE,"E5.49.0");Q31=makeQuery(id+"F0.imprint","IMPRINT",FACE,{"disambiguationData":[TD([[makeQuery(id+"F0.imprint","IMPRINT",EDGE,{"derivedFrom":subQ0}),1.0]])]});}
            var Q32;
            {var subQ0=sQuery(id+"F0.wireOp",EDGE,"E5.48.0");Q32=makeQuery(id+"F0.imprint","IMPRINT",FACE,{"disambiguationData":[TD([[makeQuery(id+"F0.imprint","IMPRINT",EDGE,{"derivedFrom":subQ0}),1.0]])]});}
            var Q33;
            {var subQ0=sQuery(id+"F0.wireOp",EDGE,"E5.46.0");Q33=makeQuery(id+"F0.imprint","IMPRINT",FACE,{"disambiguationData":[TD([[makeQuery(id+"F0.imprint","IMPRINT",EDGE,{"derivedFrom":subQ0}),1.0]])]});}
            var Q34;
            {var subQ0=sQuery(id+"F0.wireOp",EDGE,"E5.45.0");Q34=makeQuery(id+"F0.imprint","IMPRINT",FACE,{"disambiguationData":[TD([[makeQuery(id+"F0.imprint","IMPRINT",EDGE,{"derivedFrom":subQ0}),1.0]])]});}
            var Q35;
            {var subQ0=sQuery(id+"F0.wireOp",EDGE,"E5.47.0");Q35=makeQuery(id+"F0.imprint","IMPRINT",FACE,{"disambiguationData":[TD([[makeQuery(id+"F0.imprint","IMPRINT",EDGE,{"derivedFrom":subQ0}),1.0]])]});}
            var Q36;
            {var subQ0=sQuery(id+"F0.wireOp",EDGE,"E5.44.0");Q36=makeQuery(id+"F0.imprint","IMPRINT",FACE,{"disambiguationData":[TD([[makeQuery(id+"F0.imprint","IMPRINT",EDGE,{"derivedFrom":subQ0}),1.0]])]});}
            var Q37;
            {var subQ0=sQuery(id+"F0.wireOp",EDGE,"E5.42.0");Q37=makeQuery(id+"F0.imprint","IMPRINT",FACE,{"disambiguationData":[TD([[makeQuery(id+"F0.imprint","IMPRINT",EDGE,{"derivedFrom":subQ0}),1.0]])]});}
            var Q38;
            {var subQ0=sQuery(id+"F0.wireOp",EDGE,"E5.40.0");Q38=makeQuery(id+"F0.imprint","IMPRINT",FACE,{"disambiguationData":[TD([[makeQuery(id+"F0.imprint","IMPRINT",EDGE,{"derivedFrom":subQ0}),1.0]])]});}
            var Q39;
            {var subQ0=sQuery(id+"F0.wireOp",EDGE,"E5.39.0");Q39=makeQuery(id+"F0.imprint","IMPRINT",FACE,{"disambiguationData":[TD([[makeQuery(id+"F0.imprint","IMPRINT",EDGE,{"derivedFrom":subQ0}),1.0]])]});}
            var Q40;
            {var subQ0=sQuery(id+"F0.wireOp",EDGE,"E5.38.0");Q40=makeQuery(id+"F0.imprint","IMPRINT",FACE,{"disambiguationData":[TD([[makeQuery(id+"F0.imprint","IMPRINT",EDGE,{"derivedFrom":subQ0}),1.0]])]});}
            var Q41;
            {var subQ0=sQuery(id+"F0.wireOp",EDGE,"E5.41.0");Q41=makeQuery(id+"F0.imprint","IMPRINT",FACE,{"disambiguationData":[TD([[makeQuery(id+"F0.imprint","IMPRINT",EDGE,{"derivedFrom":subQ0}),1.0]])]});}
            var Q42;
            {var subQ0=sQuery(id+"F0.wireOp",EDGE,"E5.43.0");Q42=makeQuery(id+"F0.imprint","IMPRINT",FACE,{"disambiguationData":[TD([[makeQuery(id+"F0.imprint","IMPRINT",EDGE,{"derivedFrom":subQ0}),1.0]])]});}
            var Q43;
            {var subQ0=sQuery(id+"F0.wireOp",EDGE,"E5.37.0");Q43=makeQuery(id+"F0.imprint","IMPRINT",FACE,{"disambiguationData":[TD([[makeQuery(id+"F0.imprint","IMPRINT",EDGE,{"derivedFrom":subQ0}),1.0]])]});}
            var Q44;
            {var subQ0=sQuery(id+"F0.wireOp",EDGE,"E5.36.0");Q44=makeQuery(id+"F0.imprint","IMPRINT",FACE,{"disambiguationData":[TD([[makeQuery(id+"F0.imprint","IMPRINT",EDGE,{"derivedFrom":subQ0}),1.0]])]});}
            var Q45;
            {var subQ0=sQuery(id+"F0.wireOp",EDGE,"E5.35.0");Q45=makeQuery(id+"F0.imprint","IMPRINT",FACE,{"disambiguationData":[TD([[makeQuery(id+"F0.imprint","IMPRINT",EDGE,{"derivedFrom":subQ0}),1.0]])]});}
            var Q46;
            {var subQ0=sQuery(id+"F0.wireOp",EDGE,"E5.34.0");Q46=makeQuery(id+"F0.imprint","IMPRINT",FACE,{"disambiguationData":[TD([[makeQuery(id+"F0.imprint","IMPRINT",EDGE,{"derivedFrom":subQ0}),1.0]])]});}
            var Q47;
            {var subQ0=sQuery(id+"F0.wireOp",EDGE,"E5.33.0");Q47=makeQuery(id+"F0.imprint","IMPRINT",FACE,{"disambiguationData":[TD([[makeQuery(id+"F0.imprint","IMPRINT",EDGE,{"derivedFrom":subQ0}),1.0]])]});}
            var Q48;
            {var subQ0=sQuery(id+"F0.wireOp",EDGE,"E5.32.0");Q48=makeQuery(id+"F0.imprint","IMPRINT",FACE,{"disambiguationData":[TD([[makeQuery(id+"F0.imprint","IMPRINT",EDGE,{"derivedFrom":subQ0}),1.0]])]});}
            var Q49;
            {var subQ0=sQuery(id+"F0.wireOp",EDGE,"E5.31.0");Q49=makeQuery(id+"F0.imprint","IMPRINT",FACE,{"disambiguationData":[TD([[makeQuery(id+"F0.imprint","IMPRINT",EDGE,{"derivedFrom":subQ0}),1.0]])]});}
            var Q50;
            {var subQ0=sQuery(id+"F0.wireOp",EDGE,"E5.30.0");Q50=makeQuery(id+"F0.imprint","IMPRINT",FACE,{"disambiguationData":[TD([[makeQuery(id+"F0.imprint","IMPRINT",EDGE,{"derivedFrom":subQ0}),1.0]])]});}
            var Q51;
            {var subQ0=sQuery(id+"F0.wireOp",EDGE,"E5.29.0");Q51=makeQuery(id+"F0.imprint","IMPRINT",FACE,{"disambiguationData":[TD([[makeQuery(id+"F0.imprint","IMPRINT",EDGE,{"derivedFrom":subQ0}),1.0]])]});}
            var Q52;
            {var subQ0=sQuery(id+"F0.wireOp",EDGE,"E5.28.0");Q52=makeQuery(id+"F0.imprint","IMPRINT",FACE,{"disambiguationData":[TD([[makeQuery(id+"F0.imprint","IMPRINT",EDGE,{"derivedFrom":subQ0}),1.0]])]});}
            var Q53;
            {var subQ0=sQuery(id+"F0.wireOp",EDGE,"E5.28.0");Q53=makeQuery(id+"F0.imprint","IMPRINT",FACE,{"disambiguationData":[TD([[makeQuery(id+"F0.imprint","IMPRINT",EDGE,{"derivedFrom":subQ0}),1.0]])]});}
            var Q54;
            {var subQ0=sQuery(id+"F0.wireOp",EDGE,"E5.27.0");Q54=makeQuery(id+"F0.imprint","IMPRINT",FACE,{"disambiguationData":[TD([[makeQuery(id+"F0.imprint","IMPRINT",EDGE,{"derivedFrom":subQ0}),1.0]])]});}
            var Q55;
            {var subQ0=sQuery(id+"F0.wireOp",EDGE,"E5.26.0");Q55=makeQuery(id+"F0.imprint","IMPRINT",FACE,{"disambiguationData":[TD([[makeQuery(id+"F0.imprint","IMPRINT",EDGE,{"derivedFrom":subQ0}),1.0]])]});}
            var Q56;
            {var subQ0=sQuery(id+"F0.wireOp",EDGE,"E5.25.0");Q56=makeQuery(id+"F0.imprint","IMPRINT",FACE,{"disambiguationData":[TD([[makeQuery(id+"F0.imprint","IMPRINT",EDGE,{"derivedFrom":subQ0}),1.0]])]});}
            var Q57;
            {var subQ0=sQuery(id+"F0.wireOp",EDGE,"E5.24.0");Q57=makeQuery(id+"F0.imprint","IMPRINT",FACE,{"disambiguationData":[TD([[makeQuery(id+"F0.imprint","IMPRINT",EDGE,{"derivedFrom":subQ0}),1.0]])]});}
            var Q58;
            {var subQ0=sQuery(id+"F0.wireOp",EDGE,"E5.21.0");Q58=makeQuery(id+"F0.imprint","IMPRINT",FACE,{"disambiguationData":[TD([[makeQuery(id+"F0.imprint","IMPRINT",EDGE,{"derivedFrom":subQ0}),1.0]])]});}
            var Q59;
            {var subQ0=sQuery(id+"F0.wireOp",EDGE,"E5.20.0");Q59=makeQuery(id+"F0.imprint","IMPRINT",FACE,{"disambiguationData":[TD([[makeQuery(id+"F0.imprint","IMPRINT",EDGE,{"derivedFrom":subQ0}),1.0]])]});}
            var Q60;
            {var subQ0=sQuery(id+"F0.wireOp",EDGE,"E5.22.0");Q60=makeQuery(id+"F0.imprint","IMPRINT",FACE,{"disambiguationData":[TD([[makeQuery(id+"F0.imprint","IMPRINT",EDGE,{"derivedFrom":subQ0}),1.0]])]});}
            var Q61;
            {var subQ0=sQuery(id+"F0.wireOp",EDGE,"E5.23.0");Q61=makeQuery(id+"F0.imprint","IMPRINT",FACE,{"disambiguationData":[TD([[makeQuery(id+"F0.imprint","IMPRINT",EDGE,{"derivedFrom":subQ0}),1.0]])]});}
            var Q62;
            {var subQ0=sQuery(id+"F0.wireOp",EDGE,"E5.19.0");Q62=makeQuery(id+"F0.imprint","IMPRINT",FACE,{"disambiguationData":[TD([[makeQuery(id+"F0.imprint","IMPRINT",EDGE,{"derivedFrom":subQ0}),1.0]])]});}
            var Q63;
            {var subQ0=sQuery(id+"F0.wireOp",EDGE,"E5.18.0");Q63=makeQuery(id+"F0.imprint","IMPRINT",FACE,{"disambiguationData":[TD([[makeQuery(id+"F0.imprint","IMPRINT",EDGE,{"derivedFrom":subQ0}),1.0]])]});}
            var Q64;
            {var subQ0=sQuery(id+"F0.wireOp",EDGE,"E5.17.0");Q64=makeQuery(id+"F0.imprint","IMPRINT",FACE,{"disambiguationData":[TD([[makeQuery(id+"F0.imprint","IMPRINT",EDGE,{"derivedFrom":subQ0}),1.0]])]});}
            var Q65;
            {var subQ0=sQuery(id+"F0.wireOp",EDGE,"E5.16.0");Q65=makeQuery(id+"F0.imprint","IMPRINT",FACE,{"disambiguationData":[TD([[makeQuery(id+"F0.imprint","IMPRINT",EDGE,{"derivedFrom":subQ0}),1.0]])]});}
            var Q66;
            {var subQ0=sQuery(id+"F0.wireOp",EDGE,"E5.15.0");Q66=makeQuery(id+"F0.imprint","IMPRINT",FACE,{"disambiguationData":[TD([[makeQuery(id+"F0.imprint","IMPRINT",EDGE,{"derivedFrom":subQ0}),1.0]])]});}
            var Q67;
            {var subQ0=sQuery(id+"F0.wireOp",EDGE,"E5.14.0");Q67=makeQuery(id+"F0.imprint","IMPRINT",FACE,{"disambiguationData":[TD([[makeQuery(id+"F0.imprint","IMPRINT",EDGE,{"derivedFrom":subQ0}),1.0]])]});}
            var Q68;
            {var subQ0=sQuery(id+"F0.wireOp",EDGE,"E5.13.0");Q68=makeQuery(id+"F0.imprint","IMPRINT",FACE,{"disambiguationData":[TD([[makeQuery(id+"F0.imprint","IMPRINT",EDGE,{"derivedFrom":subQ0}),1.0]])]});}
            var Q69;
            {var subQ0=sQuery(id+"F0.wireOp",EDGE,"E5.12.0");Q69=makeQuery(id+"F0.imprint","IMPRINT",FACE,{"disambiguationData":[TD([[makeQuery(id+"F0.imprint","IMPRINT",EDGE,{"derivedFrom":subQ0}),1.0]])]});}
            var Q70;
            {var subQ0=sQuery(id+"F0.wireOp",EDGE,"E5.10.0");Q70=makeQuery(id+"F0.imprint","IMPRINT",FACE,{"disambiguationData":[TD([[makeQuery(id+"F0.imprint","IMPRINT",EDGE,{"derivedFrom":subQ0}),1.0]])]});}
            var Q71;
            {var subQ0=sQuery(id+"F0.wireOp",EDGE,"E5.8.0");Q71=makeQuery(id+"F0.imprint","IMPRINT",FACE,{"disambiguationData":[TD([[makeQuery(id+"F0.imprint","IMPRINT",EDGE,{"derivedFrom":subQ0}),1.0]])]});}
            var Q72;
            {var subQ0=sQuery(id+"F0.wireOp",EDGE,"E5.7.0");Q72=makeQuery(id+"F0.imprint","IMPRINT",FACE,{"disambiguationData":[TD([[makeQuery(id+"F0.imprint","IMPRINT",EDGE,{"derivedFrom":subQ0}),1.0]])]});}
            var Q73;
            {var subQ0=sQuery(id+"F0.wireOp",EDGE,"E5.6.0");Q73=makeQuery(id+"F0.imprint","IMPRINT",FACE,{"disambiguationData":[TD([[makeQuery(id+"F0.imprint","IMPRINT",EDGE,{"derivedFrom":subQ0}),1.0]])]});}
            var Q74;
            {var subQ0=sQuery(id+"F0.wireOp",EDGE,"E5.5.0");Q74=makeQuery(id+"F0.imprint","IMPRINT",FACE,{"disambiguationData":[TD([[makeQuery(id+"F0.imprint","IMPRINT",EDGE,{"derivedFrom":subQ0}),1.0]])]});}
            var Q75;
            {var subQ0=sQuery(id+"F0.wireOp",EDGE,"E5.11.0");Q75=makeQuery(id+"F0.imprint","IMPRINT",FACE,{"disambiguationData":[TD([[makeQuery(id+"F0.imprint","IMPRINT",EDGE,{"derivedFrom":subQ0}),1.0]])]});}
            var Q76;
            {var subQ0=sQuery(id+"F0.wireOp",EDGE,"E5.9.0");Q76=makeQuery(id+"F0.imprint","IMPRINT",FACE,{"disambiguationData":[TD([[makeQuery(id+"F0.imprint","IMPRINT",EDGE,{"derivedFrom":subQ0}),1.0]])]});}
            var Q77;
            {var subQ0=sQuery(id+"F0.wireOp",EDGE,"E5.4.0");Q77=makeQuery(id+"F0.imprint","IMPRINT",FACE,{"disambiguationData":[TD([[makeQuery(id+"F0.imprint","IMPRINT",EDGE,{"derivedFrom":subQ0}),1.0]])]});}
            var Q78;
            {var subQ0=sQuery(id+"F0.wireOp",EDGE,"E5.3.0");Q78=makeQuery(id+"F0.imprint","IMPRINT",FACE,{"disambiguationData":[TD([[makeQuery(id+"F0.imprint","IMPRINT",EDGE,{"derivedFrom":subQ0}),1.0]])]});}
            var Q79;
            {var subQ0=sQuery(id+"F0.wireOp",EDGE,"E5.2.0");Q79=makeQuery(id+"F0.imprint","IMPRINT",FACE,{"disambiguationData":[TD([[makeQuery(id+"F0.imprint","IMPRINT",EDGE,{"derivedFrom":subQ0}),1.0]])]});}
            var Q80;
            {var subQ0=sQuery(id+"F0.wireOp",EDGE,"E5.1.0");Q80=makeQuery(id+"F0.imprint","IMPRINT",FACE,{"disambiguationData":[TD([[makeQuery(id+"F0.imprint","IMPRINT",EDGE,{"derivedFrom":subQ0}),1.0]])]});}
            var Q81;
            {var subQ0=sQuery(id+"F0.wireOp",EDGE,"E5.66.0");Q81=makeQuery(id+"F0.imprint","IMPRINT",FACE,{"disambiguationData":[TD([[makeQuery(id+"F0.imprint","IMPRINT",EDGE,{"derivedFrom":subQ0}),1.0]])]});}
            extrude(context, id + "F1", {"entities" : qUnion([Q0, Q1, Q2, Q3, Q4, Q5, Q6, Q7, Q8, Q9, Q10, Q11, Q12, Q13, Q14, Q15, Q16, Q17, Q18, Q19, Q20, Q21, Q22, Q23, Q24, Q25, Q26, Q27, Q28, Q29, Q30, Q31, Q32, Q33, Q34, Q35, Q36, Q37, Q38, Q39, Q40, Q41, Q42, Q43, Q44, Q45, Q46, Q47, Q48, Q49, Q50, Q51, Q52, Q53, Q54, Q55, Q56, Q57, Q58, Q59, Q60, Q61, Q62, Q63, Q64, Q65, Q66, Q67, Q68, Q69, Q70, Q71, Q72, Q73, Q74, Q75, Q76, Q77, Q78, Q79, Q80, Q81]), "depth" : 5 * mm, "offsetDistance" : 25 * mm});
        }
    });
